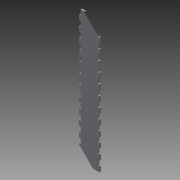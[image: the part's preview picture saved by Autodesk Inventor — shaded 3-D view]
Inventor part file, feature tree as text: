
AUTODESK INVENTOR PART (.ipt)
format: ipt  version: 2015 (Build 190159000, 159)  size: 204,288 bytes
history: native  units: in
note: dims shown in document units (in); Inventor stores cm internally (conversion verified against a paired STEP export)
features: reference x4, extrude x1, sketch x1
ambient origin geometry x8: Origin, YZ Plane, XZ Plane, XY Plane, X Axis, Y Axis, Z Axis, Center Point
bodies: Solid1 (feature_tree)
feature tree (6):
  extrude  "Extrusion1"  Depth=0.7874in
  sketch  "Sketch1"  dims[d0=0.25in d1=0.0in d16=0.7874in d17=0.7874in d18=0.7874in d19=0.7874in d20=0.7874in d21=0.7874in d22=0.7874in d23=0.7874in d24=0.7874in d25=0.7874in d26=0.7874in d27=0.7874in d28=0.7874in d29=0.7874in d30=0.7874in d31=0.7874in d32=0.7874in d33=0.7874in d34=0.7874in d35=0.7874in d36=0.7874in d37=0.7874in d38=0.7874in d39=0.7874in]
  reference  "Reference2"
  reference  "Reference3"
  reference  "Reference4"
  reference  "Reference5"
